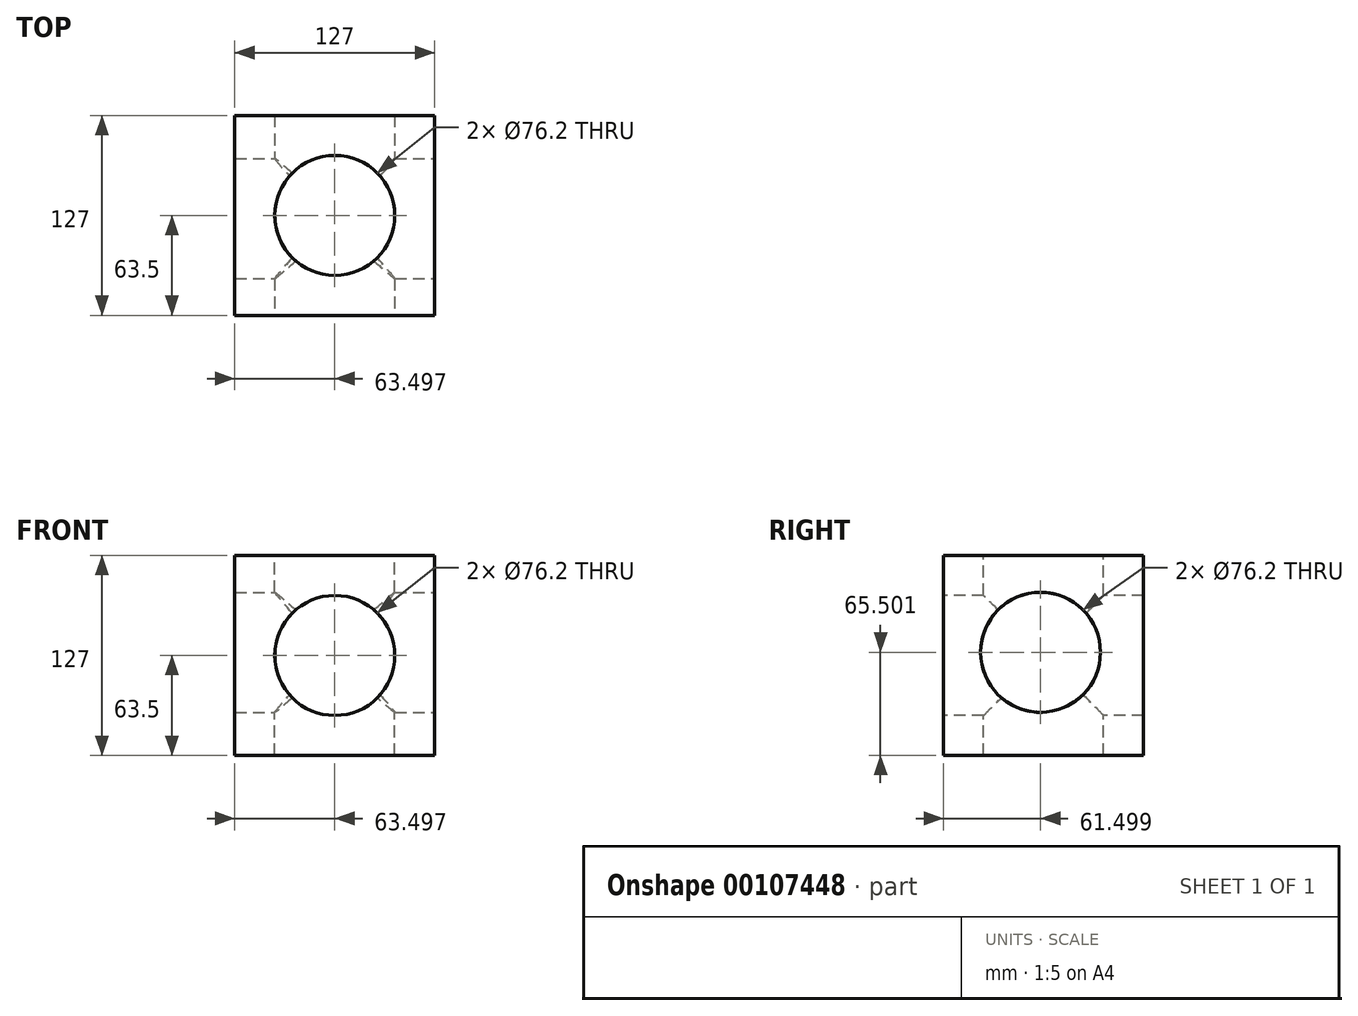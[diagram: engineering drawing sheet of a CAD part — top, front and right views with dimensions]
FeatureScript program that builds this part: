
annotation { "Feature Type Name" : "Feature", "Feature Type Description" : "" }
export const myFeature = defineFeature(function(context is Context, id is Id, definition is map)
    precondition{}
    {
        {
            var Q0;
            Q0=qCreatedBy(makeId("Front.planeOp"),FACE);
            var sketch = newSketch(context, id + "F0", { "sketchPlane" : qUnion([Q0])});
            skLineSegment(sketch, "E0.bottom", {"start": v(-51.13, 45.38) * mm, "end": v(75.87, 45.38) * mm});
            skLineSegment(sketch, "E0.top", {"start": v(-51.13, -81.62) * mm, "end": v(75.87, -81.62) * mm});
            skLineSegment(sketch, "E0.left", {"start": v(-51.13, 45.38) * mm, "end": v(-51.13, -81.62) * mm});
            skLineSegment(sketch, "E0.right", {"start": v(75.87, 45.38) * mm, "end": v(75.87, -81.62) * mm});
            skSolve(sketch);
        }
        {
            var Q0;
            Q0 = qSketchRegion(id + "F0", true);
            extrude(context, id + "F1", {"entities" : qUnion([Q0]), "depth" : 127 * mm});
        }
        {
            var Q0;
            Q0=makeQuery(id+"F1.opExtrude","CAP_FACE",FACE,{"disambiguationData":[OSD([sQuery(id+"F0.wireOp",EDGE,"E0.bottom"),sQuery(id+"F0.wireOp",EDGE,"E0.top"),sQuery(id+"F0.wireOp",EDGE,"E0.left"),sQuery(id+"F0.wireOp",EDGE,"E0.right")])],"isStart":false});
            var sketch = newSketch(context, id + "F2", { "sketchPlane" : qUnion([Q0])});
            skLineSegment(sketch, "E1", {"start": v(-51.13, 45.38) * mm, "end": v(75.87, -81.62) * mm, "construction": true});
            skCircle(sketch, "E2", {"center": v(12.37, -18.12) * mm, "radius": 38.1 * mm});
            skSolve(sketch);
        }
        {
            var Q0;
            Q0=makeQuery(id+"F2.imprint","IMPRINT",FACE,{"disambiguationData":[TD([[makeQuery(id+"F2.imprint","IMPRINT",EDGE,{"derivedFrom":sQuery(id+"F2.wireOp",EDGE,"E2")}),1.0]])]});
            extrude(context, id + "F3", {"entities" : qUnion([Q0]), "operationType" : NewBodyOperationType.REMOVE, "endBound" : BoundingType.THROUGH_ALL, "oppositeDirection" : true, "depth" : 25.4 * mm});
        }
        {
            var Q0;
            Q0=makeQuery(id+"F1.opExtrude","SWEPT_FACE",FACE,{"disambiguationData":[OSD([sQuery(id+"F0.wireOp",EDGE,"E0.right")])]});
            var sketch = newSketch(context, id + "F4", { "sketchPlane" : qUnion([Q0])});
            skLineSegment(sketch, "E3", {"start": v(-127, 45.38) * mm, "end": v(0, -81.62) * mm, "construction": true});
            skCircle(sketch, "E4", {"center": v(-65.5, -16.12) * mm, "radius": 38.1 * mm});
            skSolve(sketch);
        }
        {
            var Q0;
            Q0=makeQuery(id+"F4.imprint","IMPRINT",FACE,{"disambiguationData":[TD([[makeQuery(id+"F4.imprint","IMPRINT",EDGE,{"derivedFrom":sQuery(id+"F4.wireOp",EDGE,"E4")}),1.0]])]});
            extrude(context, id + "F5", {"entities" : qUnion([Q0]), "operationType" : NewBodyOperationType.REMOVE, "endBound" : BoundingType.THROUGH_ALL, "oppositeDirection" : true, "depth" : 25.4 * mm});
        }
        {
            var Q0;
            Q0=makeQuery(id+"F1.opExtrude","SWEPT_FACE",FACE,{"disambiguationData":[OSD([sQuery(id+"F0.wireOp",EDGE,"E0.bottom")])]});
            var sketch = newSketch(context, id + "F6", { "sketchPlane" : qUnion([Q0])});
            skLineSegment(sketch, "E5", {"start": v(-51.13, 0) * mm, "end": v(75.87, -127) * mm, "construction": true});
            skCircle(sketch, "E6", {"center": v(12.37, -63.5) * mm, "radius": 38.1 * mm});
            skSolve(sketch);
        }
        {
            var Q0;
            Q0=makeQuery(id+"F6.imprint","IMPRINT",FACE,{"disambiguationData":[TD([[makeQuery(id+"F6.imprint","IMPRINT",EDGE,{"derivedFrom":sQuery(id+"F6.wireOp",EDGE,"E6")}),1.0]])]});
            extrude(context, id + "F7", {"entities" : qUnion([Q0]), "operationType" : NewBodyOperationType.REMOVE, "endBound" : BoundingType.THROUGH_ALL, "oppositeDirection" : true, "depth" : 25.4 * mm});
        }
    });
